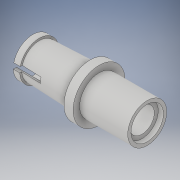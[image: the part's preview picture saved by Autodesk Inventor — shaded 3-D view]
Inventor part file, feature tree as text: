
AUTODESK INVENTOR PART (.ipt)
format: ipt  version: 2017 (Build 210142000, 142)  size: 177,152 bytes
history: native  units: in
note: dims shown in document units (in); Inventor stores cm internally (conversion verified against a paired STEP export)
features: sketch x2, revolve x1, plane x1, extrude x1
ambient origin geometry x8: Origin, YZ Plane, XZ Plane, XY Plane, X Axis, Y Axis, Z Axis, Center Point
bodies: Solid1 (feature_tree)
feature tree (5):
  revolve  "Revolution1"  [1 undecoded]
  plane  "Work Plane1"
  extrude  "Extrusion1"  Depth=0.05in
  sketch  "Sketch1"  dims[d0=0.88in d4=0.025in]
  sketch  "Sketch2"  dims[d7=0.03in d11=0.05in d15=0.33in d17=0.03in d18=0.05in d19=0.015in d21=90.0deg d22=0.04in d23=0.37in d24=0.37in d25=0.44in d26=0.63in d27=0.075in d28=0.125in d29=0.325in d30=0.5321in d31=0.0254in d32=0.0643in d33=0.0in d34=0.275in d35=0.2777in d36=0.88in d37=0.88in d38=90.0deg d44=0.2in d45=0.04in d46=0.1163in d47=0.25in d48=0.0in]
note: 1 required parameter value undecoded (feature->parameter linkage not recoverable at this tier; creation-order binding heuristic only, values carry confidence <= 0.55)
